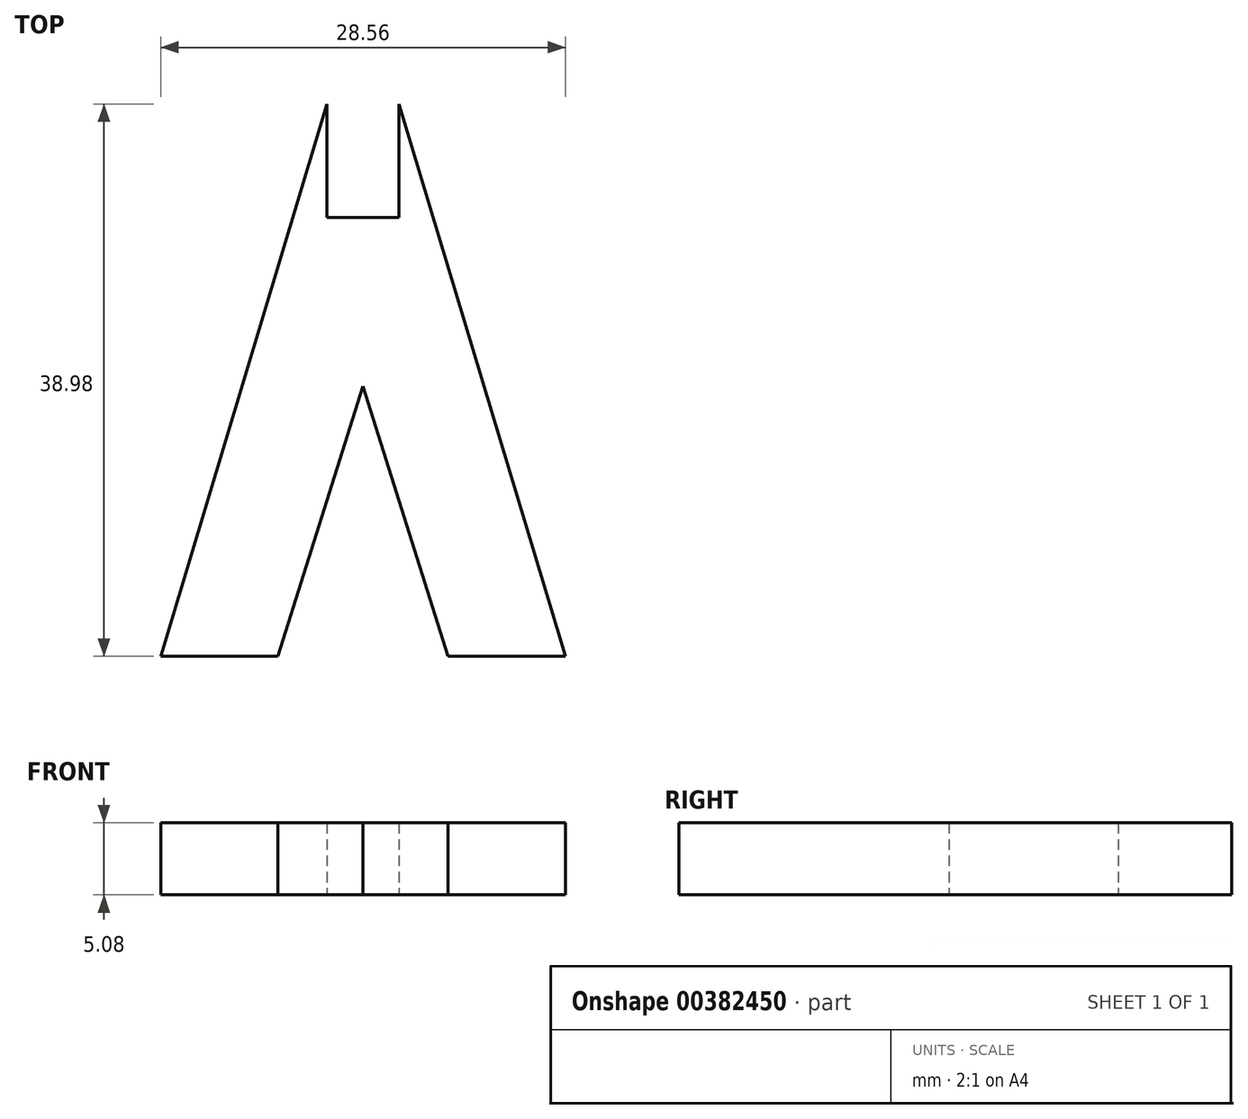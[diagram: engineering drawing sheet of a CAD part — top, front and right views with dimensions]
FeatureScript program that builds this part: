
annotation { "Feature Type Name" : "Feature", "Feature Type Description" : "" }
export const myFeature = defineFeature(function(context is Context, id is Id, definition is map)
    precondition{}
    {
        {
            var Q0;
            Q0=qCreatedBy(makeId("Top.planeOp"),FACE);
            var sketch = newSketch(context, id + "F0", { "sketchPlane" : qUnion([Q0])});
            skLineSegment(sketch, "E0", {"start": v(150.5, 3.14) * mm, "end": v(150.5, -35.7) * mm, "construction": true});
            skLineSegment(sketch, "E1", {"start": v(0, 0) * mm, "end": v(0, 38.1) * mm, "construction": true});
            skLineSegment(sketch, "E2", {"start": v(0, 30.98) * mm, "end": v(2.54, 30.98) * mm});
            skLineSegment(sketch, "E3", {"start": v(2.54, 30.98) * mm, "end": v(2.54, 38.98) * mm});
            skLineSegment(sketch, "E4", {"start": v(2.54, 38.98) * mm, "end": v(14.28, 0) * mm});
            skLineSegment(sketch, "E5", {"start": v(14.28, 0) * mm, "end": v(6, 0) * mm});
            skLineSegment(sketch, "E6", {"start": v(6, 0) * mm, "end": v(0, 19.05) * mm});
            skLineSegment(sketch, "E7.MirrorCS", {"start": v(-2.54, 38.98) * mm, "end": v(-14.28, 0) * mm});
            skLineSegment(sketch, "E8.MirrorCS", {"start": v(0, 30.98) * mm, "end": v(-2.54, 30.98) * mm});
            skLineSegment(sketch, "E9.MirrorCS", {"start": v(-2.54, 30.98) * mm, "end": v(-2.54, 38.98) * mm});
            skLineSegment(sketch, "E10.MirrorCS", {"start": v(-6, 0) * mm, "end": v(0, 19.05) * mm});
            skLineSegment(sketch, "E11.MirrorCS", {"start": v(-14.28, 0) * mm, "end": v(-6, 0) * mm});
            skSolve(sketch);
        }
        {
            var Q0;
            Q0 = qSketchRegion(id + "F0", true);
            extrude(context, id + "F1", {"entities" : qUnion([Q0]), "depth" : 5.08 * mm});
        }
    });
